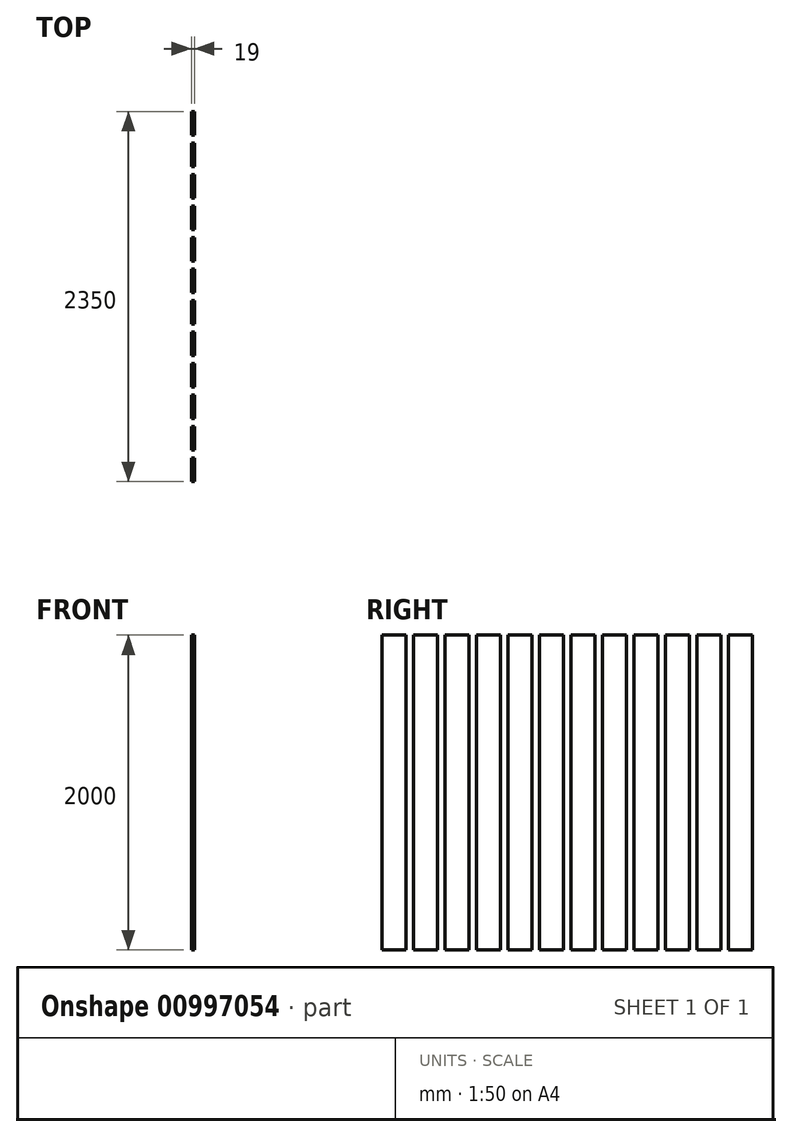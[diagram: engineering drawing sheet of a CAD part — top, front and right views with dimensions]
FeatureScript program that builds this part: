
annotation { "Feature Type Name" : "Feature", "Feature Type Description" : "" }
export const myFeature = defineFeature(function(context is Context, id is Id, definition is map)
    precondition{}
    {
        {
            var Q0;
            Q0=qCreatedBy(makeId("Top.planeOp"),FACE);
            var sketch = newSketch(context, id + "F0", { "sketchPlane" : qUnion([Q0])});
            skLineSegment(sketch, "E0.bottom", {"start": v(-97.89, 150) * mm, "end": v(-78.89, 150) * mm});
            skLineSegment(sketch, "E0.top", {"start": v(-97.89, 0) * mm, "end": v(-78.89, 0) * mm});
            skLineSegment(sketch, "E0.left", {"start": v(-97.89, 150) * mm, "end": v(-97.89, 0) * mm});
            skLineSegment(sketch, "E0.right", {"start": v(-78.89, 150) * mm, "end": v(-78.89, 0) * mm});
            skSolve(sketch);
        }
        {
            var Q0;
            Q0 = qSketchRegion(id + "F0", true);
            extrude(context, id + "F1", {"entities" : qUnion([Q0]), "depth" : 2000 * mm, "offsetDistance" : 25 * mm});
        }
        {
            var Q0;
            Q0=makeQuery(id+"F1.opExtrude","SWEPT_BODY",BODY,{"disambiguationData":[OSD([sQuery(id+"F0.wireOp",EDGE,"E0.bottom"),sQuery(id+"F0.wireOp",EDGE,"E0.top"),sQuery(id+"F0.wireOp",EDGE,"E0.left"),sQuery(id+"F0.wireOp",EDGE,"E0.right")])]});
            transform(context, id + "F2", {"entities" : qUnion([Q0]), "transformType" : TransformType.TRANSLATION_3D, "dx" : 0 * mm, "dy" : 200 * mm, "dz" : 0 * mm, "makeCopy" : true});
        }
        {
            var Q0;
            Q0=makeQuery(id+"F2.opPattern","COPY",BODY,{"derivedFrom":makeQuery(id+"F1.opExtrude","SWEPT_BODY",BODY,{"disambiguationData":[OSD([sQuery(id+"F0.wireOp",EDGE,"E0.bottom"),sQuery(id+"F0.wireOp",EDGE,"E0.top"),sQuery(id+"F0.wireOp",EDGE,"E0.left"),sQuery(id+"F0.wireOp",EDGE,"E0.right")])]}),"instanceName":"1"});
            transform(context, id + "F3", {"entities" : qUnion([Q0]), "transformType" : TransformType.TRANSLATION_3D, "dx" : 0 * mm, "dy" : 200 * mm, "dz" : 0 * mm, "makeCopy" : true});
        }
        {
            var Q0;
            Q0=makeQuery(id+"F3.opPattern","COPY",BODY,{"derivedFrom":makeQuery(id+"F2.opPattern","COPY",BODY,{"derivedFrom":makeQuery(id+"F1.opExtrude","SWEPT_BODY",BODY,{"disambiguationData":[OSD([sQuery(id+"F0.wireOp",EDGE,"E0.bottom"),sQuery(id+"F0.wireOp",EDGE,"E0.top"),sQuery(id+"F0.wireOp",EDGE,"E0.left"),sQuery(id+"F0.wireOp",EDGE,"E0.right")])]}),"instanceName":"1"}),"instanceName":"1"});
            transform(context, id + "F4", {"entities" : qUnion([Q0]), "transformType" : TransformType.TRANSLATION_3D, "dx" : 0 * mm, "dy" : 200 * mm, "dz" : 0 * mm, "makeCopy" : true});
        }
        {
            var Q0;
            Q0=makeQuery(id+"F4.opPattern","COPY",BODY,{"derivedFrom":makeQuery(id+"F3.opPattern","COPY",BODY,{"derivedFrom":makeQuery(id+"F2.opPattern","COPY",BODY,{"derivedFrom":makeQuery(id+"F1.opExtrude","SWEPT_BODY",BODY,{"disambiguationData":[OSD([sQuery(id+"F0.wireOp",EDGE,"E0.bottom"),sQuery(id+"F0.wireOp",EDGE,"E0.top"),sQuery(id+"F0.wireOp",EDGE,"E0.left"),sQuery(id+"F0.wireOp",EDGE,"E0.right")])]}),"instanceName":"1"}),"instanceName":"1"}),"instanceName":"1"});
            transform(context, id + "F5", {"entities" : qUnion([Q0]), "transformType" : TransformType.TRANSLATION_3D, "dx" : 0 * mm, "dy" : 200 * mm, "dz" : 0 * mm, "makeCopy" : true});
        }
        {
            var Q0;
            Q0=makeQuery(id+"F5.opPattern","COPY",BODY,{"derivedFrom":makeQuery(id+"F4.opPattern","COPY",BODY,{"derivedFrom":makeQuery(id+"F3.opPattern","COPY",BODY,{"derivedFrom":makeQuery(id+"F2.opPattern","COPY",BODY,{"derivedFrom":makeQuery(id+"F1.opExtrude","SWEPT_BODY",BODY,{"disambiguationData":[OSD([sQuery(id+"F0.wireOp",EDGE,"E0.bottom"),sQuery(id+"F0.wireOp",EDGE,"E0.top"),sQuery(id+"F0.wireOp",EDGE,"E0.left"),sQuery(id+"F0.wireOp",EDGE,"E0.right")])]}),"instanceName":"1"}),"instanceName":"1"}),"instanceName":"1"}),"instanceName":"1"});
            transform(context, id + "F6", {"entities" : qUnion([Q0]), "transformType" : TransformType.TRANSLATION_3D, "dx" : 0 * mm, "dy" : 200 * mm, "dz" : 0 * mm, "makeCopy" : true});
        }
        {
            var Q0;
            Q0=makeQuery(id+"F6.opPattern","COPY",BODY,{"derivedFrom":makeQuery(id+"F5.opPattern","COPY",BODY,{"derivedFrom":makeQuery(id+"F4.opPattern","COPY",BODY,{"derivedFrom":makeQuery(id+"F3.opPattern","COPY",BODY,{"derivedFrom":makeQuery(id+"F2.opPattern","COPY",BODY,{"derivedFrom":makeQuery(id+"F1.opExtrude","SWEPT_BODY",BODY,{"disambiguationData":[OSD([sQuery(id+"F0.wireOp",EDGE,"E0.bottom"),sQuery(id+"F0.wireOp",EDGE,"E0.top"),sQuery(id+"F0.wireOp",EDGE,"E0.left"),sQuery(id+"F0.wireOp",EDGE,"E0.right")])]}),"instanceName":"1"}),"instanceName":"1"}),"instanceName":"1"}),"instanceName":"1"}),"instanceName":"1"});
            transform(context, id + "F7", {"entities" : qUnion([Q0]), "transformType" : TransformType.TRANSLATION_3D, "dx" : 0 * mm, "dy" : 200 * mm, "dz" : 0 * mm, "makeCopy" : true});
        }
        {
            var Q0;
            Q0=makeQuery(id+"F7.opPattern","COPY",BODY,{"derivedFrom":makeQuery(id+"F6.opPattern","COPY",BODY,{"derivedFrom":makeQuery(id+"F5.opPattern","COPY",BODY,{"derivedFrom":makeQuery(id+"F4.opPattern","COPY",BODY,{"derivedFrom":makeQuery(id+"F3.opPattern","COPY",BODY,{"derivedFrom":makeQuery(id+"F2.opPattern","COPY",BODY,{"derivedFrom":makeQuery(id+"F1.opExtrude","SWEPT_BODY",BODY,{"disambiguationData":[OSD([sQuery(id+"F0.wireOp",EDGE,"E0.bottom"),sQuery(id+"F0.wireOp",EDGE,"E0.top"),sQuery(id+"F0.wireOp",EDGE,"E0.left"),sQuery(id+"F0.wireOp",EDGE,"E0.right")])]}),"instanceName":"1"}),"instanceName":"1"}),"instanceName":"1"}),"instanceName":"1"}),"instanceName":"1"}),"instanceName":"1"});
            transform(context, id + "F8", {"entities" : qUnion([Q0]), "transformType" : TransformType.TRANSLATION_3D, "dx" : 0 * mm, "dy" : 200 * mm, "dz" : 0 * mm, "makeCopy" : true});
        }
        {
            var Q0;
            Q0=makeQuery(id+"F8.opPattern","COPY",BODY,{"derivedFrom":makeQuery(id+"F7.opPattern","COPY",BODY,{"derivedFrom":makeQuery(id+"F6.opPattern","COPY",BODY,{"derivedFrom":makeQuery(id+"F5.opPattern","COPY",BODY,{"derivedFrom":makeQuery(id+"F4.opPattern","COPY",BODY,{"derivedFrom":makeQuery(id+"F3.opPattern","COPY",BODY,{"derivedFrom":makeQuery(id+"F2.opPattern","COPY",BODY,{"derivedFrom":makeQuery(id+"F1.opExtrude","SWEPT_BODY",BODY,{"disambiguationData":[OSD([sQuery(id+"F0.wireOp",EDGE,"E0.bottom"),sQuery(id+"F0.wireOp",EDGE,"E0.top"),sQuery(id+"F0.wireOp",EDGE,"E0.left"),sQuery(id+"F0.wireOp",EDGE,"E0.right")])]}),"instanceName":"1"}),"instanceName":"1"}),"instanceName":"1"}),"instanceName":"1"}),"instanceName":"1"}),"instanceName":"1"}),"instanceName":"1"});
            transform(context, id + "F9", {"entities" : qUnion([Q0]), "transformType" : TransformType.TRANSLATION_3D, "dx" : 0 * mm, "dy" : 200 * mm, "dz" : 0 * mm, "makeCopy" : true});
        }
        {
            var Q0;
            Q0=makeQuery(id+"F9.opPattern","COPY",BODY,{"derivedFrom":makeQuery(id+"F8.opPattern","COPY",BODY,{"derivedFrom":makeQuery(id+"F7.opPattern","COPY",BODY,{"derivedFrom":makeQuery(id+"F6.opPattern","COPY",BODY,{"derivedFrom":makeQuery(id+"F5.opPattern","COPY",BODY,{"derivedFrom":makeQuery(id+"F4.opPattern","COPY",BODY,{"derivedFrom":makeQuery(id+"F3.opPattern","COPY",BODY,{"derivedFrom":makeQuery(id+"F2.opPattern","COPY",BODY,{"derivedFrom":makeQuery(id+"F1.opExtrude","SWEPT_BODY",BODY,{"disambiguationData":[OSD([sQuery(id+"F0.wireOp",EDGE,"E0.bottom"),sQuery(id+"F0.wireOp",EDGE,"E0.top"),sQuery(id+"F0.wireOp",EDGE,"E0.left"),sQuery(id+"F0.wireOp",EDGE,"E0.right")])]}),"instanceName":"1"}),"instanceName":"1"}),"instanceName":"1"}),"instanceName":"1"}),"instanceName":"1"}),"instanceName":"1"}),"instanceName":"1"}),"instanceName":"1"});
            transform(context, id + "F10", {"entities" : qUnion([Q0]), "transformType" : TransformType.TRANSLATION_3D, "dx" : 0 * mm, "dy" : 200 * mm, "dz" : 0 * mm, "makeCopy" : true});
        }
        {
            var Q0;
            Q0=makeQuery(id+"F10.opPattern","COPY",BODY,{"derivedFrom":makeQuery(id+"F9.opPattern","COPY",BODY,{"derivedFrom":makeQuery(id+"F8.opPattern","COPY",BODY,{"derivedFrom":makeQuery(id+"F7.opPattern","COPY",BODY,{"derivedFrom":makeQuery(id+"F6.opPattern","COPY",BODY,{"derivedFrom":makeQuery(id+"F5.opPattern","COPY",BODY,{"derivedFrom":makeQuery(id+"F4.opPattern","COPY",BODY,{"derivedFrom":makeQuery(id+"F3.opPattern","COPY",BODY,{"derivedFrom":makeQuery(id+"F2.opPattern","COPY",BODY,{"derivedFrom":makeQuery(id+"F1.opExtrude","SWEPT_BODY",BODY,{"disambiguationData":[OSD([sQuery(id+"F0.wireOp",EDGE,"E0.bottom"),sQuery(id+"F0.wireOp",EDGE,"E0.top"),sQuery(id+"F0.wireOp",EDGE,"E0.left"),sQuery(id+"F0.wireOp",EDGE,"E0.right")])]}),"instanceName":"1"}),"instanceName":"1"}),"instanceName":"1"}),"instanceName":"1"}),"instanceName":"1"}),"instanceName":"1"}),"instanceName":"1"}),"instanceName":"1"}),"instanceName":"1"});
            transform(context, id + "F11", {"entities" : qUnion([Q0]), "transformType" : TransformType.TRANSLATION_3D, "dx" : 0 * mm, "dy" : 200 * mm, "dz" : 0 * mm, "makeCopy" : true});
        }
        {
            var Q0;
            Q0=makeQuery(id+"F11.opPattern","COPY",BODY,{"derivedFrom":makeQuery(id+"F10.opPattern","COPY",BODY,{"derivedFrom":makeQuery(id+"F9.opPattern","COPY",BODY,{"derivedFrom":makeQuery(id+"F8.opPattern","COPY",BODY,{"derivedFrom":makeQuery(id+"F7.opPattern","COPY",BODY,{"derivedFrom":makeQuery(id+"F6.opPattern","COPY",BODY,{"derivedFrom":makeQuery(id+"F5.opPattern","COPY",BODY,{"derivedFrom":makeQuery(id+"F4.opPattern","COPY",BODY,{"derivedFrom":makeQuery(id+"F3.opPattern","COPY",BODY,{"derivedFrom":makeQuery(id+"F2.opPattern","COPY",BODY,{"derivedFrom":makeQuery(id+"F1.opExtrude","SWEPT_BODY",BODY,{"disambiguationData":[OSD([sQuery(id+"F0.wireOp",EDGE,"E0.bottom"),sQuery(id+"F0.wireOp",EDGE,"E0.top"),sQuery(id+"F0.wireOp",EDGE,"E0.left"),sQuery(id+"F0.wireOp",EDGE,"E0.right")])]}),"instanceName":"1"}),"instanceName":"1"}),"instanceName":"1"}),"instanceName":"1"}),"instanceName":"1"}),"instanceName":"1"}),"instanceName":"1"}),"instanceName":"1"}),"instanceName":"1"}),"instanceName":"1"});
            transform(context, id + "F12", {"entities" : qUnion([Q0]), "transformType" : TransformType.TRANSLATION_3D, "dx" : 0 * mm, "dy" : 200 * mm, "dz" : 0 * mm, "makeCopy" : true});
        }
    });
